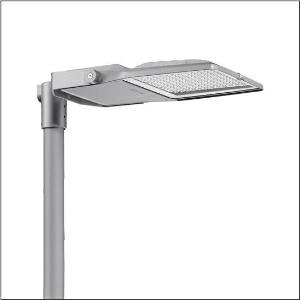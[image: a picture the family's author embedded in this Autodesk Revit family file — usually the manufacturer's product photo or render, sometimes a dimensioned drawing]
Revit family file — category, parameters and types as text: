
# Revit family: floodlight_fl_21_iq_midi___pl33t_5xa7781e6f3a_cd97
name_source: partatom
category: Lighting Fixtures
units: mm (PartAtom-declared; Revit-internal decimal feet)

## family parameters
Cut with Voids When Loaded = No
Host = Face
Light Source = No
Part Type = Normal
Room Calculation Point = No
Round Connector Dimension = Use Diameter
Shared = No

## types (1)
- --- (1 x LED, 21270 lm, 208.1 W, 5700K)
    Apparent Load = 208 VA
    CIE Flux Codes = 26 75 99 100 100
    Color Rendering = 90
    Color Temperature = 5700K
    Default Elevation = 1800 mm
    Description = Floodlight FL 21 iQ midi, floodlight, primary light control with lens, of PMMA, primary optical cover: protective disc, of toughened safety glass, transparent, light distribution: PL33T, light emission: direct distribution, installation type: surface-mounted, LED, High Power LED, rated luminous flux: 21.270lm, luminous efficacy: 102lm/W, light colour: 957, colour temperature: 5700K, control gear: ECG iQ, control: optimised constant luminous flux control (CLO 2.0), Desk-Remote (wireless, voltage-free reading and setting of iQ features in the workshop via application-optimized NFC function/RFID function), Light-Fading, Smart-Wire, Night-Set, Lumen-Switch, Temp-Guard, Auto-Match, with terminal, 6-pole, mains connection: 220..240V, AC, 50/60Hz, start of lifetime: 208W, end of service life: 227W, reduction: 90W, luminaire housing, of diecast aluminium, powder-coated, Siteco® metallic grey (DB 702S), corrosivity category C5 mid according to DIN EN ISO 12944, sealing non-destructively replaceable, please order mast flange separately, mast bracket, of steel, galvanised, powder-coated, Siteco® metallic grey (DB 702S), protection rating (complete): IP66, insulation class (complete): insulation class II (safety insulation), certification: CE, protection symbol: D, impact resistance: IK08, permissible operating ambient temperature: -40..+40°C, permissible operating ambient temperature for outdoor applications: -40..+50°C, standard: DIN EN 12944, LABS conformity tested according to VDMA 24364:2018-05, packaging unit: 1 piece

Light Distribution: PL33T
    Height = 76 mm
    Lamp = 1 x LED
    Lamp Light Flux = 21270 lm
    Lamp Power = 208.1 W
    Lamp count = 1
    Length = 657 mm
    Luminous efficacy = 102 lm/W
    Manufacturer = Siteco
    ModVariant = No
    Model = 5XA7781E6F3A
    Number of Poles = 1
    OnlyDefault = Yes
    Power Factor = 1
    Product Name = Floodlight FL 21 iQ midi | PL33T
    Product group = floodlight | pylon annexe
    ProductGroupID = 6200
    Protection Class = Protection class II
    Protection Degree = IP 66
    RLX_Detail_Level = 1
    RLX_Emergency_Light_Flux = 0 lm
    RLX_Emergency_Type = 0
    RLX_Emergency_Type_DB = No
    RlxData = <blob elided: 153677 chars, md5=f14678e8>
    Socket = socket
    Standby Power = 0 W
    System Light Flux = 21270 lm
    System Power = 208 W
    Type Comments = factory setting: luminous flux: 100 % | dim-lin: 254 | 710 mA
    Type Image = l_1007123.jpg
    URL = http://relux.com
    VarID = @adj_033767
    Voltage = 0 V
    Weight = 0.00 kg
    Width = 442 mm

## geometry (parser evidence)
native form markers: Blend x4, Sweep x13
no freeform markers — native parametric forms only
